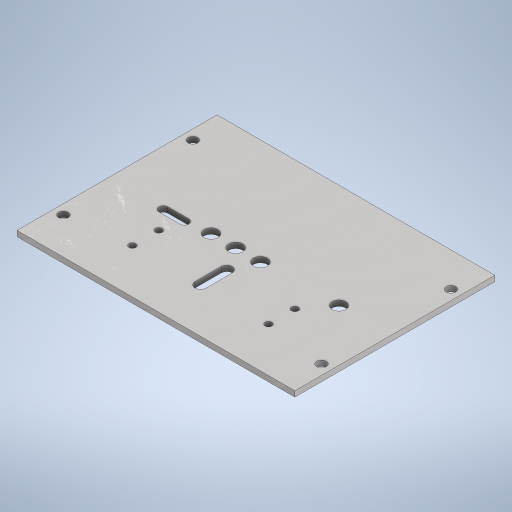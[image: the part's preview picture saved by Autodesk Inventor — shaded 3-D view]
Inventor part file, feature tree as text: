
AUTODESK INVENTOR PART (.ipt)
format: ipt  version: 2023 (Build 270158000, 158)  size: 421,376 bytes
history: native  units: mm
features: reference x19, extrude x10, sketch x10, other x7, projected_geometry x3
ambient origin geometry x8: Origin, YZ Plane, XZ Plane, XY Plane, X Axis, Y Axis, Z Axis, Center Point
bodies: Body1 (feature_tree)
feature tree (49):
  other  "Bryła1"
  extrude  "Wyciągnięcie proste1"  Depth=100.0mm
  extrude  "Wyciągnięcie proste2"  Depth=70.0mm
  extrude  "Wyciągnięcie proste3"  Depth=0.5mm TaperAngle=0.0deg
  extrude  "Wyciągnięcie proste4"  Depth=0.5mm
  extrude  "Wyciągnięcie proste5"  Depth=0.5mm
  extrude  "Wyciągnięcie proste6"  Depth=0.5mm
  extrude  "Wyciągnięcie proste7"  Depth=0.5mm
  extrude  "Wyciągnięcie proste8"  Depth=1.3mm
  extrude  "Wyciągnięcie proste9"  TaperAngle=0.0deg  [1 undecoded]
  extrude  "Wyciągnięcie proste10"  TaperAngle=0.0deg  [1 undecoded]
  sketch  "Szkic1"
  sketch  "Szkic2"
  reference  "Odniesienie1"
  reference  "Odniesienie2"
  reference  "Odniesienie3"
  reference  "Odniesienie4"
  reference  "Odniesienie5"
  reference  "Odniesienie6"
  reference  "Odniesienie7"
  reference  "Odniesienie8"
  reference  "Odniesienie9"
  sketch  "Szkic3"
  reference  "Odniesienie10"
  reference  "Odniesienie11"
  reference  "Odniesienie12"
  reference  "Odniesienie13"
  reference  "Odniesienie14"
  reference  "Odniesienie15"
  reference  "Odniesienie16"
  reference  "Odniesienie17"
  reference  "Odniesienie18"
  reference  "Odniesienie19"
  sketch  "Szkic4"
  projected_geometry  "Pętla rzutowana1"
  sketch  "Szkic5"
  projected_geometry  "Pętla rzutowana2"
  sketch  "Szkic6"
  sketch  "Szkic7"
  projected_geometry  "Pętla rzutowana3"
  sketch  "Szkic8"
  sketch  "Szkic9"
  sketch  "Szkic10"
  other  "<userpath>\Desktop\MojeRoboty\Stefan\mechanics 2\STEFAN.iam"
  other  "STEFAN.iam"
  other  "board_up:1"
  other  "sciana_prawa_nowa_MIR:1"
  other  "sciana_prawa_nowa:1"
  other  "uchwyt_serw:1"
note: 2 required parameter values undecoded (feature->parameter linkage not recoverable at this tier; creation-order binding heuristic only, values carry confidence <= 0.55)
